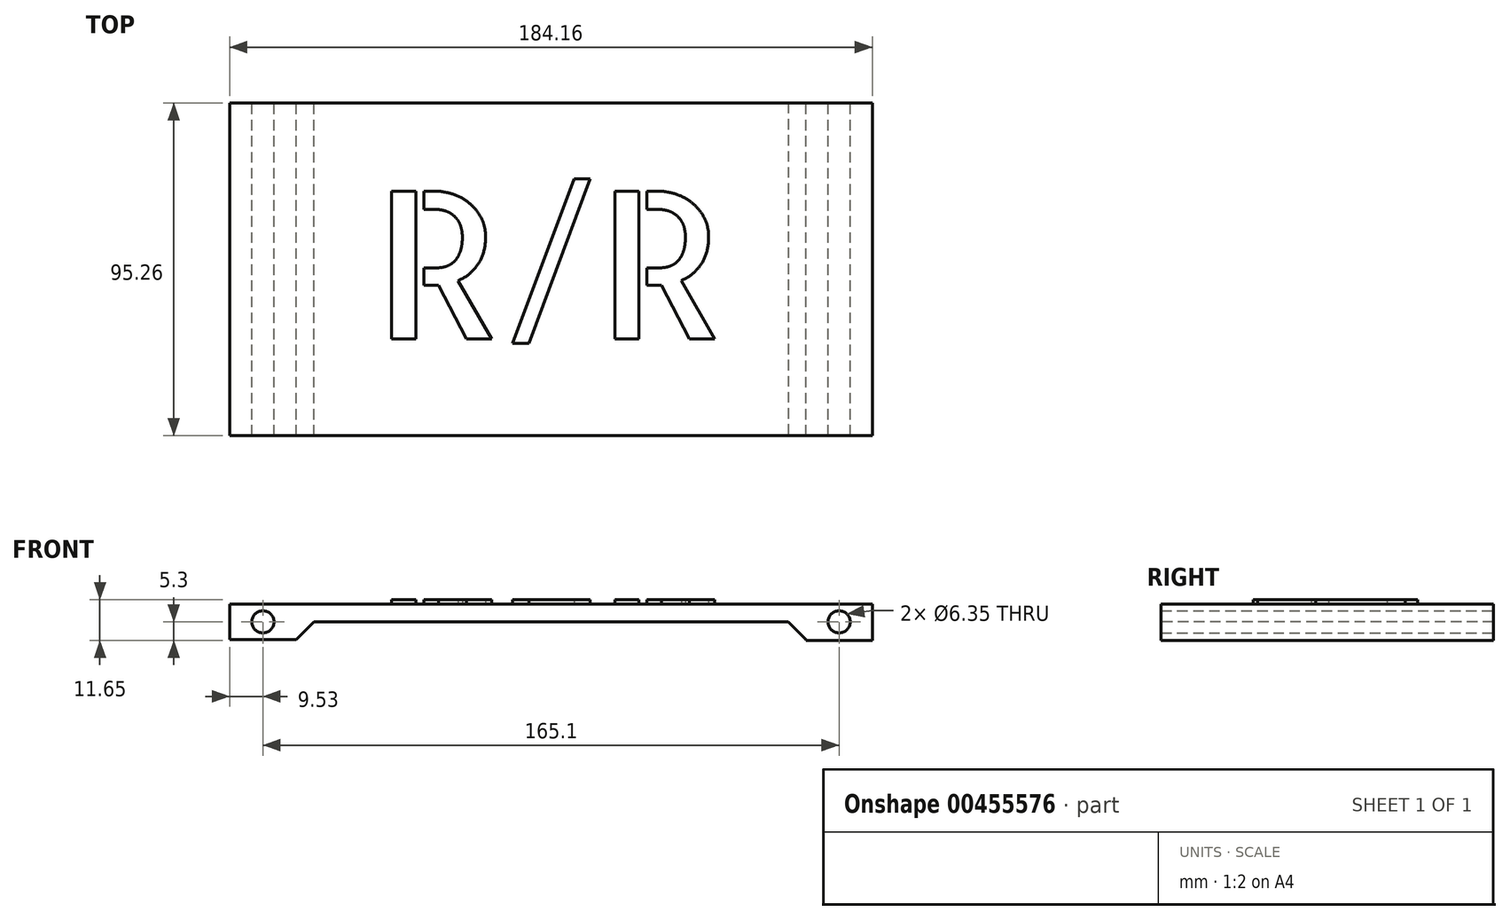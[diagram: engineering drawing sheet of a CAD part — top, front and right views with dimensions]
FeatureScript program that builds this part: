
annotation { "Feature Type Name" : "Feature", "Feature Type Description" : "" }
export const myFeature = defineFeature(function(context is Context, id is Id, definition is map)
    precondition{}
    {
        {
            var Q0;
            Q0=qCreatedBy(makeId("Front.planeOp"),FACE);
            var sketch = newSketch(context, id + "F0", { "sketchPlane" : qUnion([Q0])});
            skLineSegment(sketch, "E0.bottom", {"start": v(-92.08, 2.54) * mm, "end": v(92.08, 2.54) * mm});
            skLineSegment(sketch, "E0.top", {"start": v(-92.08, -2.54) * mm, "end": v(92.08, -2.54) * mm});
            skLineSegment(sketch, "E0.left", {"start": v(-92.08, 2.54) * mm, "end": v(-92.08, -2.54) * mm});
            skLineSegment(sketch, "E0.right", {"start": v(92.08, 2.54) * mm, "end": v(92.08, -2.54) * mm});
            skPoint(sketch, "E0.middle", {"position": v(0, 0) * mm});
            skLineSegment(sketch, "E1.bottom", {"start": v(-92.08, -2.54) * mm, "end": v(-73.03, -2.54) * mm});
            skLineSegment(sketch, "E1.top", {"start": v(-92.08, -7.62) * mm, "end": v(-73.03, -7.62) * mm});
            skLineSegment(sketch, "E1.left", {"start": v(-92.08, -2.54) * mm, "end": v(-92.08, -7.62) * mm});
            skLineSegment(sketch, "E1.right", {"start": v(-73.03, -2.54) * mm, "end": v(-73.03, -7.62) * mm});
            skCircle(sketch, "E2", {"center": v(-82.55, -2.54) * mm, "radius": 3.18 * mm});
            skLineSegment(sketch, "E3.bottom", {"start": v(92.08, -2.54) * mm, "end": v(73.03, -2.54) * mm});
            skLineSegment(sketch, "E3.top", {"start": v(92.08, -7.84) * mm, "end": v(73.03, -7.84) * mm});
            skLineSegment(sketch, "E3.left", {"start": v(92.08, -2.54) * mm, "end": v(92.08, -7.84) * mm});
            skLineSegment(sketch, "E3.right", {"start": v(73.03, -2.54) * mm, "end": v(73.03, -7.84) * mm});
            skCircle(sketch, "E4", {"center": v(82.55, -2.54) * mm, "radius": 3.18 * mm});
            skSolve(sketch);
        }
        {
            var Q0;
            Q0 = qSketchRegion(id + "F0", true);
            extrude(context, id + "F1", {"entities" : qUnion([Q0]), "endBound" : BoundingType.SYMMETRIC, "depth" : 95.25 * mm});
        }
        {
            var Q0;
            Q0=makeQuery(id+"F1.opExtrude","SWEPT_EDGE",EDGE,{"disambiguationData":[OSD([sQuery(id+"F0.wireOp",EDGE,"E0.top"),sQuery(id+"F0.wireOp",EDGE,"E1.bottom"),sQuery(id+"F0.wireOp",EDGE,"E1.right")])]});
            var Q1;
            Q1=makeQuery(id+"F1.opExtrude","SWEPT_EDGE",EDGE,{"disambiguationData":[OSD([sQuery(id+"F0.wireOp",EDGE,"E0.top"),sQuery(id+"F0.wireOp",EDGE,"E3.bottom"),sQuery(id+"F0.wireOp",EDGE,"E3.right")])]});
            chamfer(context, id + "F2", {"entities" : qUnion([Q0, Q1]), "width" : 5.08 * mm, "tangentPropagation" : true});
        }
        {
            var Q0;
            Q0=makeQuery(id+"F1.opExtrude","SWEPT_FACE",FACE,{"disambiguationData":[OSD([sQuery(id+"F0.wireOp",EDGE,"E0.bottom")])]});
            var sketch = newSketch(context, id + "F3", { "sketchPlane" : qUnion([Q0])});
            skText(sketch, "E5", { "text": "R/R", "fontName": "AllertaStencil-Regular.ttf"});
            const initialGuessF3  = {"E5": [-0.05081, -0.0199, 1, 0, 0.0423]};
            skSetInitialGuess(sketch, initialGuessF3);
            skSolve(sketch);
        }
        {
            var Q0;
            Q0 = qSketchRegion(id + "F3", true);
            extrude(context, id + "F4", {"entities" : qUnion([Q0]), "operationType" : NewBodyOperationType.ADD, "endBound" : BoundingType.SYMMETRIC, "depth" : 2.54 * mm});
        }
    });
